# Revit family: Sink-Vessel-KOHLER-Pallene-K-14016_1
name_source: partatom
category: Plumbing Fixtures
revit_build: Autodesk Revit 2015 (Build: 20140606_1530(x64)
units: mm (PartAtom-declared; Revit-internal decimal feet)

## types (1)
- B11-Ice
    ADA Compliant = Yes
    Assembly Code = D2010400
    CW Connection = No
    Cold Water Inlet = Cold Water Inlet
    Date Modified = 12/03/2018
    Default Elevation = 34"
    Description = Vessel glass bathroom sink
    Drain Included = No
    Finish = Kohler-Glass-B11-Ice
    HW Connection = No
    Height = 4 1/16"
    Hot Water Inlet = Hot Water Inlet
    Length = 18 7/8"
    Manufacturer = KOHLER Co.
    MasterFormat 1995 = 15410
    MasterFormat 2004 = 22.41.16
    Material = Glass
    Model = K-14016-B11
    Product Documentation Link = http://www.us.kohler.com
    Product Name = Pallene
    Product Page URL = http://www.us.kohler.com
    URL = https://www.us.kohler.com
    Vent Connection = No
    Waste Connection = Yes
    Waste Water Outlet = Waste Water Outlet
    Width = 18 7/8"

## geometry (parser evidence)
native form markers: Sweep x5
no freeform markers — native parametric forms only
